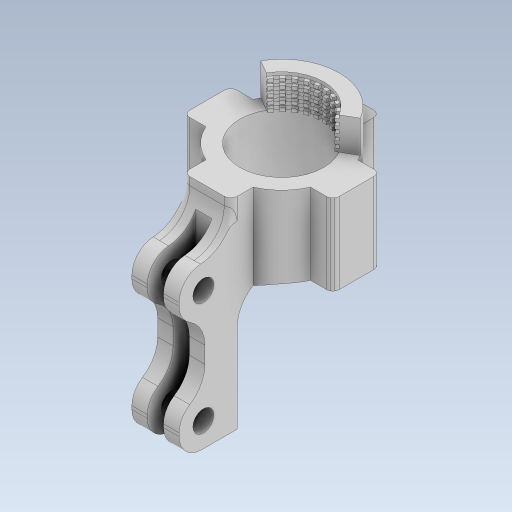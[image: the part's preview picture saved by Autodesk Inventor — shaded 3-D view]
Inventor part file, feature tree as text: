
AUTODESK INVENTOR PART (.ipt)
format: ipt  version: 2023 (Build 270158000, 158)  size: 1,098,240 bytes
history: native  units: in
note: dims shown in document units (in); Inventor stores cm internally (conversion verified against a paired STEP export)
features: sketch x6, extrude x5, projected_geometry x2, revolve x1, fillet x1
ambient origin geometry x8: Origin, YZ Plane, XZ Plane, XY Plane, X Axis, Y Axis, Z Axis, Center Point
bodies: Solid1 (feature_tree)
feature tree (15):
  extrude  "Extrusion1"  Depth=0.9843in TaperAngle=0.0deg
  extrude  "Extrusion2"  Depth=0.3937in TaperAngle=0.0deg
  extrude  "Extrusion3"  Depth=7.874in TaperAngle=120.0deg
  revolve  "Revolution1"  [1 undecoded]
  extrude  "Extrusion14"  Depth=1.9685in
  fillet  "Fillet3"  Radius=0.2559in
  extrude  "Extrusion15"  Depth=0.3937in
  sketch  "Sketch1"  dims[d0=1.0236in d1=0.9843in d2=0.0in]
  sketch  "Sketch2"  dims[d3=120.0deg d4=0.3937in d5=0.0in]
  sketch  "Sketch3"  dims[d6=0.0394in d7=7.874in d9=120.0deg]
  sketch  "Sketch4"  dims[d11=0.3937in d12=0.0in d14=3.937in d16=0.0394in d17=0.3937in d19=0.3937in]
  sketch  "Sketch26"  dims[d21=360.0deg d107=1.9685in d108=0.2559in]
  sketch  "Sketch27"  dims[d109=1.378in d111=0.3937in d112=0.9843in d113=0.9843in d114=0.0in d115=0.2756in d116=0.3937in d117=0.1969in d118=0.5906in d119=0.0in d91=0.0344in d92=0.0344in d93=0.0197in d94=0.0344in]
  projected_geometry  "Projected Loop10"
  projected_geometry  "Projected Loop11"
note: 1 required parameter value undecoded (feature->parameter linkage not recoverable at this tier; creation-order binding heuristic only, values carry confidence <= 0.55)
